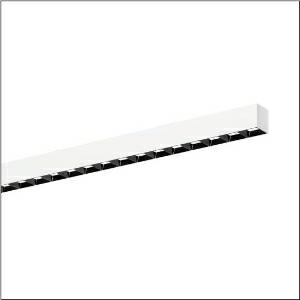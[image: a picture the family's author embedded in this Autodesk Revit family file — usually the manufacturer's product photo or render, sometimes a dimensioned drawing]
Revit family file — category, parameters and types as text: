
# Revit family: silica_r__21_51mx24da34wb_1271
name_source: partatom
category: Lighting Fixtures
units: mm (PartAtom-declared; Revit-internal decimal feet)

## family parameters
Cut with Voids When Loaded = No
Host = Face
Light Source = No
Part Type = Normal
Room Calculation Point = No
Round Connector Dimension = Use Diameter
Shared = No

## types (1)
- --- (1 x LED, 4320 lm, 32.1 W, 3000K)
    Apparent Load = 32 VA
    CIE Flux Codes = 74 94 99 100 100
    Color Rendering = 80
    Color Temperature = 3000K
    Default Elevation = 1800 mm
    Description = Silica® 21, office luminaire, primary light control with darklight reflector, of PMMA, black, CAT 2 (L<= 3000cd/m²), light emission: direct distribution, primary light characteristic: asymmetric, installation type: surface-mounted, LED, rated luminous flux: 4.320lm, luminous efficacy: 135lm/W, light colour: 830, colour temperature: 3000K, control gear: DALI 2, with terminal, 3+2-pole, max. 2.5mm², mains connection: 220..240V, AC, 50/60Hz, rated input power: 32.1W, luminaire housing, of aluminium, traffic white (RAL 9016), length: 1.204mm, width: 53mm, height: 53mm, protection rating (complete): IP20, insulation class (complete): insulation class I (protective earthing), certification: CE, permissible operating ambient temperature: 0..+35°C, standard: EN 50419, packaging unit: 1 piece
    Height = 53 mm
    Lamp = 1 x LED
    Lamp Light Flux = 4320 lm
    Lamp Power = 32.1 W
    Lamp count = 1
    Length = 1204 mm
    Luminous efficacy = 135 lm/W
    Manufacturer = Siteco
    ModVariant = No
    Model = 51MX24DA34WB
    Mounting Place = Ceiling
    Mounting Type = Surface mounted
    Number of Poles = 1
    OnlyDefault = Yes
    Power Factor = 1
    Product Name = Silica® 21
    Product group = office luminaire | ceiling mounted
    ProductGroupID = 302
    Protection Class = Protection class I
    Protection Degree = IP 20
    RLX_Detail_Level = 1
    RLX_Emergency_Light_Flux = 0 lm
    RLX_Emergency_Type = 0
    RLX_Emergency_Type_DB = No
    RlxData = <blob elided: 41897 chars, md5=f6106033>
    Socket = socket
    Standby Power = 0 W
    System Light Flux = 4320 lm
    System Power = 32 W
    Type Comments = factory setting: luminous flux: 100 % | dim-lin: 254 | 448 mA
    Type Image = l_1335873.jpg
    URL = http://relux.com
    VarID = @adj_123244
    Voltage = 0 V
    Weight = 0.00 kg
    Width = 53 mm

## geometry (parser evidence)
native form markers: Blend x4, Sweep x10
no freeform markers — native parametric forms only
